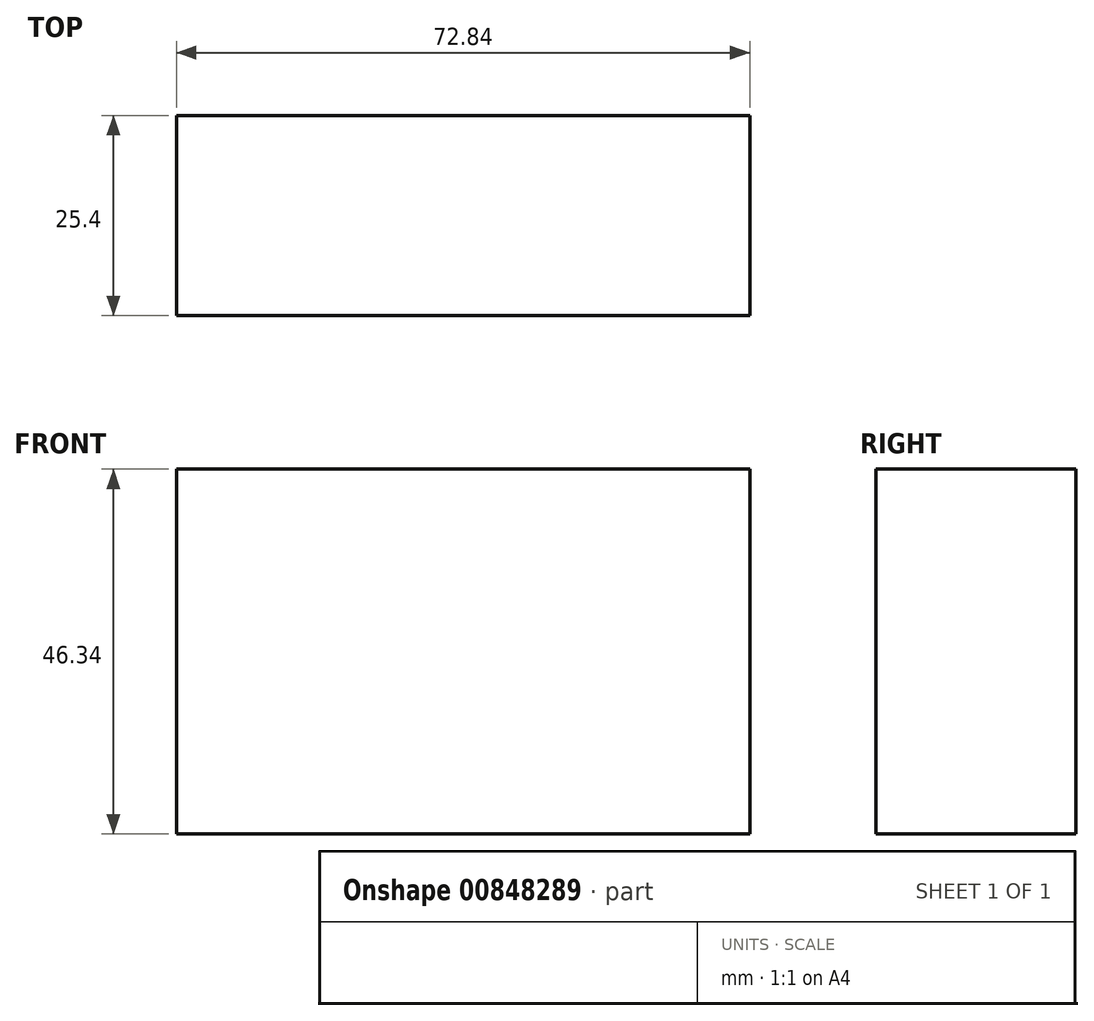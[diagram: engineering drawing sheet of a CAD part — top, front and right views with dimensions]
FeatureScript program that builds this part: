
annotation { "Feature Type Name" : "Feature", "Feature Type Description" : "" }
export const myFeature = defineFeature(function(context is Context, id is Id, definition is map)
    precondition{}
    {
        {
            var Q0;
            Q0=qCreatedBy(makeId("Front.planeOp"),FACE);
            var sketch = newSketch(context, id + "F0", { "sketchPlane" : qUnion([Q0])});
            skLineSegment(sketch, "E0.bottom", {"start": v(31.8, 0) * mm, "end": v(-41.04, 0) * mm});
            skLineSegment(sketch, "E0.top", {"start": v(31.8, 46.34) * mm, "end": v(-41.04, 46.34) * mm});
            skLineSegment(sketch, "E0.left", {"start": v(31.8, 0) * mm, "end": v(31.8, 46.34) * mm});
            skLineSegment(sketch, "E0.right", {"start": v(-41.04, 0) * mm, "end": v(-41.04, 46.34) * mm});
            skSolve(sketch);
        }
        {
            var Q0;
            Q0=makeQuery(id+"F0.imprint","IMPRINT",FACE,{"disambiguationData":[TD([[makeQuery(id+"F0.imprint","IMPRINT",EDGE,{"derivedFrom":sQuery(id+"F0.wireOp",EDGE,"E0.bottom")}),-1.0]])]});
            extrude(context, id + "F1", {"entities" : qUnion([Q0]), "depth" : 25.4 * mm, "offsetDistance" : 25.4 * mm});
        }
    });
